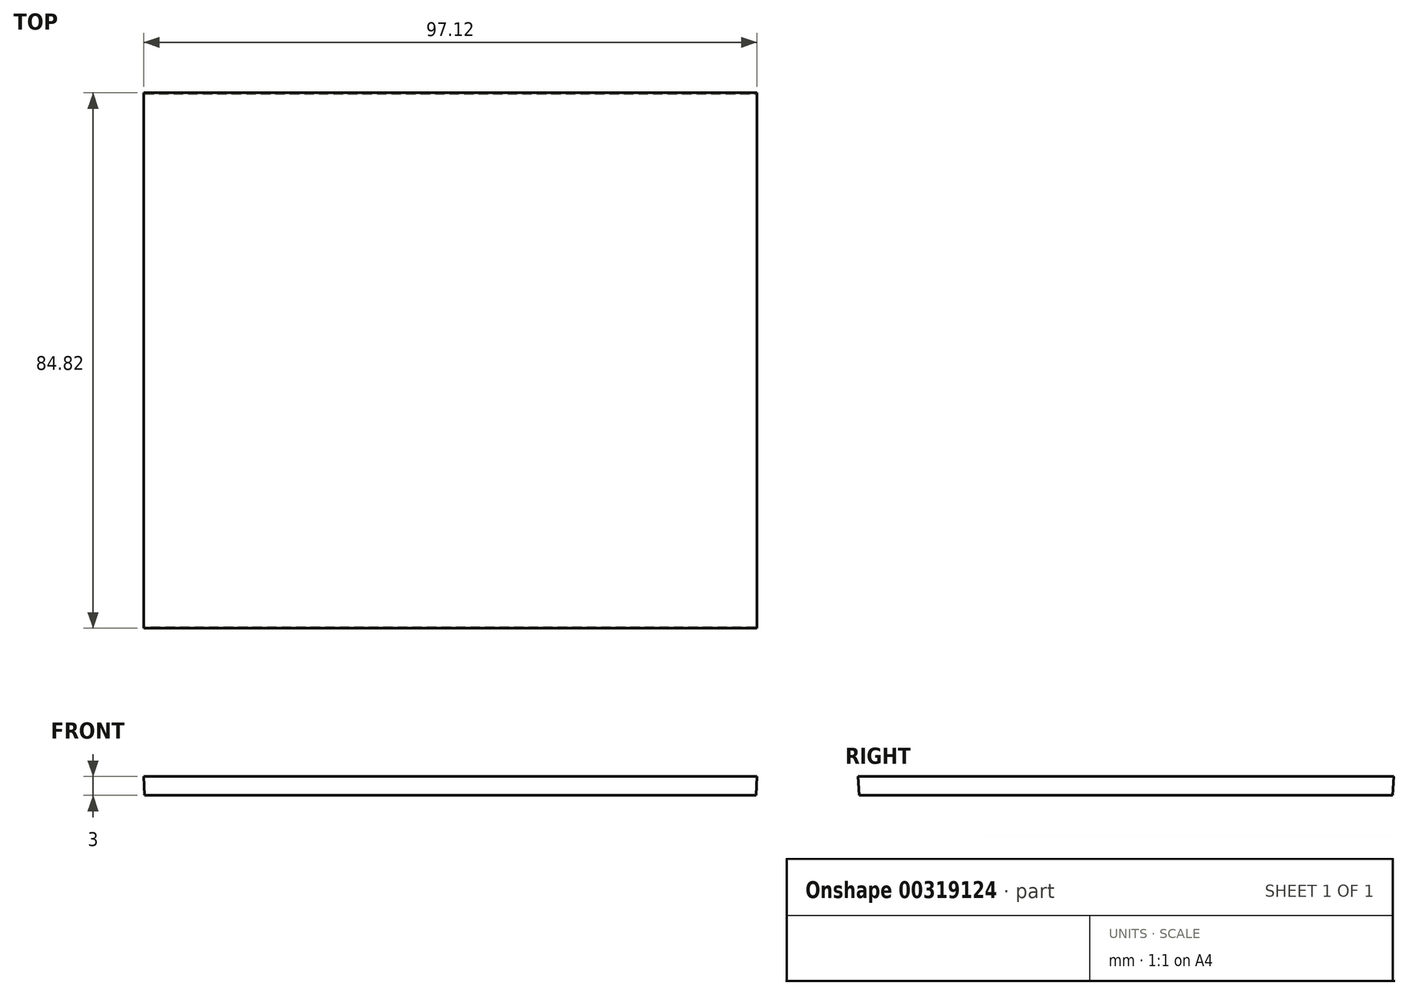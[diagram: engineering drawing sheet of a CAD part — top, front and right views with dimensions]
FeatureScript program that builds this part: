
annotation { "Feature Type Name" : "Feature", "Feature Type Description" : "" }
export const myFeature = defineFeature(function(context is Context, id is Id, definition is map)
    precondition{}
    {
        {
            var Q0;
            Q0=qCreatedBy(makeId("Top.planeOp"),FACE);
            var sketch = newSketch(context, id + "F5", { "sketchPlane" : qUnion([Q0])});
            skLineSegment(sketch, "E0.bottom", {"start": v(-39.14, 67.78) * mm, "end": v(57.66, 67.78) * mm});
            skLineSegment(sketch, "E0.top", {"start": v(-39.14, -16.72) * mm, "end": v(57.66, -16.72) * mm});
            skLineSegment(sketch, "E0.left", {"start": v(-39.14, 67.78) * mm, "end": v(-39.14, -16.72) * mm});
            skLineSegment(sketch, "E0.right", {"start": v(57.66, 67.78) * mm, "end": v(57.66, -16.72) * mm});
            skSolve(sketch);
        }
        {
            var Q0;
            Q0=makeQuery(id+"F5.imprint","IMPRINT",FACE,{"disambiguationData":[TD([[makeQuery(id+"F5.imprint","IMPRINT",EDGE,{"derivedFrom":sQuery(id+"F5.wireOp",EDGE,"E0.bottom")}),-1.0]])]});
            var sketch = newSketch(context, id + "F0", { "sketchPlane" : qUnion([Q0])});
            skSolve(sketch);
        }
        {
            var Q0;
            Q0=qSketchRegion(id+"F0",true);
            var Q1;
            Q1=makeQuery(id+"F5.imprint","IMPRINT",FACE,{"disambiguationData":[TD([[makeQuery(id+"F5.imprint","IMPRINT",EDGE,{"derivedFrom":sQuery(id+"F5.wireOp",EDGE,"E0.bottom")}),-1.0]])]});
            extrude(context, id + "F6", {"entities" : qUnion([Q0, Q1]), "depth" : 3 * mm, "hasDraft" : true, "draftAngle" : 3 * degree});
        }
    });
